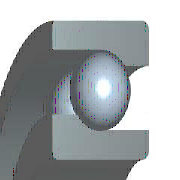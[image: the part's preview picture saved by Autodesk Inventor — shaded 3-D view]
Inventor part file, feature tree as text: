
AUTODESK INVENTOR PART (.ipt)
format: ipt  version: 2018 (Build 220112000, 112)  size: 317,952 bytes
history: native  units: mm (DEFAULTED — no unit token found)
features: other x5, plane x3, sketch x1, pattern_circular x1
ambient origin geometry x8: Origin, YZ Plane, XZ Plane, XY Plane, X Axis, Y Axis, Z Axis, Center Point
bodies: Solid1 (feature_tree)
feature tree (10):
  plane  "WorkPlane1"
  plane  "Work Plane2"
  plane  "WorkPlane2"
  other  "WorkPoint1"
  other  "WorkPoint3"
  other  "WorkPoint2"
  other  "WorkAxis1"
  sketch  "Schizzo7"
  other  "Work Axis2"
  pattern_circular  "Seriepolare1"  [2 undecoded]
note: 2 required parameter values undecoded (feature->parameter linkage not recoverable at this tier; creation-order binding heuristic only, values carry confidence <= 0.55)
